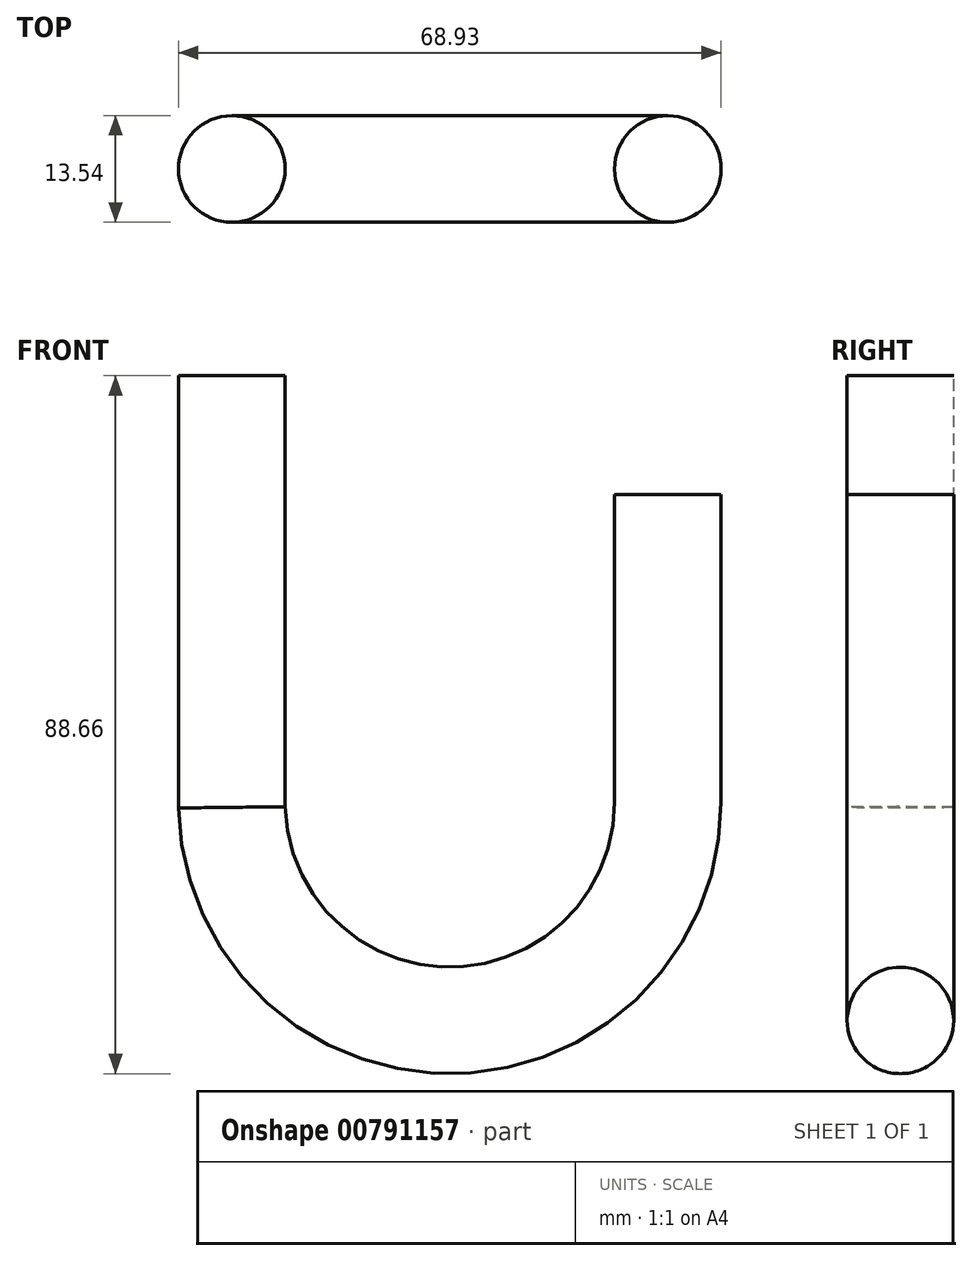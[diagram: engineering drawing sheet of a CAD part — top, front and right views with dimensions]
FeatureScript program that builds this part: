
annotation { "Feature Type Name" : "Feature", "Feature Type Description" : "" }
export const myFeature = defineFeature(function(context is Context, id is Id, definition is map)
    precondition{}
    {
        {
            var Q0;
            Q0=qCreatedBy(makeId("Front.planeOp"),FACE);
            var sketch = newSketch(context, id + "F0", { "sketchPlane" : qUnion([Q0])});
            skLineSegment(sketch, "E0", {"start": v(0, 0) * mm, "end": v(0, -39.13) * mm});
            skArc(sketch, "E1", {"start": v(0, -39.13) * mm, "mid": v(-27.38, -66.82) * mm, "end": v(-55.39, -39.77) * mm});
            skLineSegment(sketch, "E2", {"start": v(-55.39, -39.77) * mm, "end": v(-55.39, 15.06) * mm});
            skSolve(sketch);
        }
        {
            var Q0;
            Q0=qCreatedBy(makeId("Top.planeOp"),FACE);
            var sketch = newSketch(context, id + "F1", { "sketchPlane" : qUnion([Q0])});
            skCircle(sketch, "E3", {"center": v(0, 0) * mm, "radius": 6.77 * mm});
            skSolve(sketch);
        }
        {
            var Q0;
            Q0=makeQuery(id+"F1.imprint","IMPRINT",FACE,{"disambiguationData":[TD([[makeQuery(id+"F1.imprint","IMPRINT",EDGE,{"derivedFrom":sQuery(id+"F1.wireOp",EDGE,"E3")}),1.0]])]});
            var Q1;
            Q1=sQuery(id+"F1.wireOp",EDGE,"E3");
            var Q2;
            Q2=sQuery(id+"F0.wireOp",EDGE,"E1");
            var Q3;
            Q3=sQuery(id+"F0.wireOp",EDGE,"E0");
            var Q4;
            Q4=sQuery(id+"F0.wireOp",EDGE,"E2");
            sweep(context, id + "F2", {"profiles" : qUnion([Q0]), "surfaceProfiles" : qUnion([Q1]), "path" : qUnion([Q2, Q3, Q4])});
        }
    });
